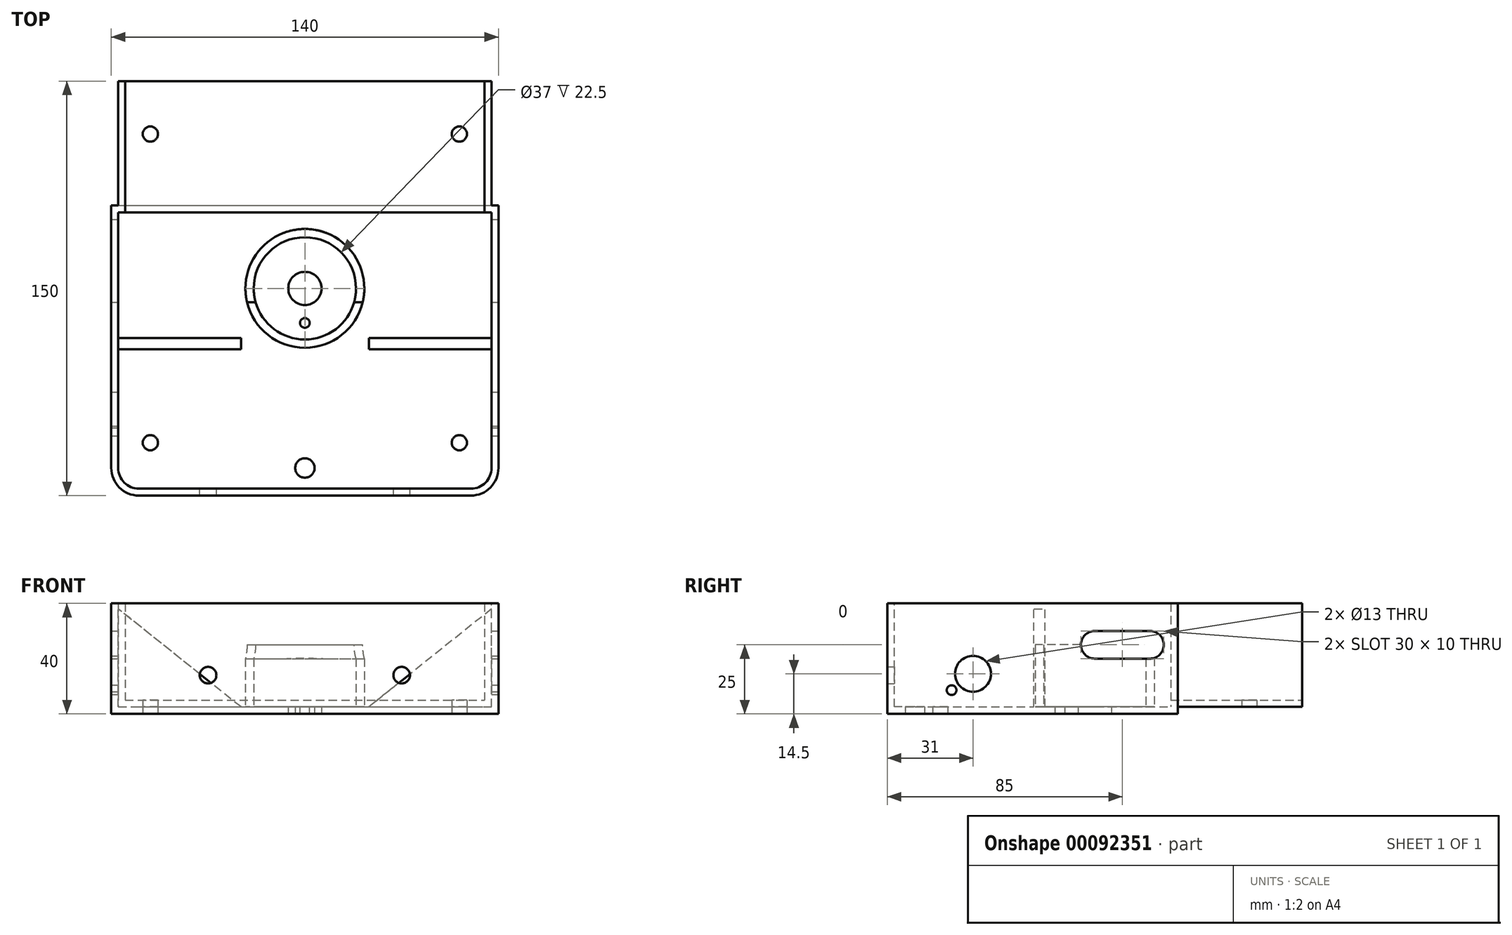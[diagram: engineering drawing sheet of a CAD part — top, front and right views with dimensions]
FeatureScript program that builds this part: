
annotation { "Feature Type Name" : "Feature", "Feature Type Description" : "" }
export const myFeature = defineFeature(function(context is Context, id is Id, definition is map)
    precondition{}
    {
        {
            var Q0;
            Q0=qCreatedBy(makeId("Top.planeOp"),FACE);
            var sketch = newSketch(context, id + "F0", { "sketchPlane" : qUnion([Q0])});
            skLineSegment(sketch, "E0.bottom", {"start": v(-70, -25) * mm, "end": v(70, -25) * mm});
            skLineSegment(sketch, "E0.top", {"start": v(-70, 125) * mm, "end": v(70, 125) * mm});
            skLineSegment(sketch, "E0.left", {"start": v(-70, -25) * mm, "end": v(-70, 125) * mm});
            skLineSegment(sketch, "E0.right", {"start": v(70, -25) * mm, "end": v(70, 125) * mm});
            skSolve(sketch);
        }
        {
            var Q0;
            Q0=makeQuery(id+"F0.imprint","IMPRINT",FACE,{"disambiguationData":[TD([[makeQuery(id+"F0.imprint","IMPRINT",EDGE,{"derivedFrom":sQuery(id+"F0.wireOp",EDGE,"E0.bottom")}),1.0]])]});
            extrude(context, id + "F1", {"entities" : qUnion([Q0]), "depth" : 40 * mm});
        }
        {
            var Q0;
            Q0=makeQuery(id+"F1.opExtrude","SWEPT_EDGE",EDGE,{"disambiguationData":[OSD([sQuery(id+"F0.wireOp",EDGE,"E0.bottom"),sQuery(id+"F0.wireOp",EDGE,"E0.left")])]});
            var Q1;
            Q1=makeQuery(id+"F1.opExtrude","SWEPT_EDGE",EDGE,{"disambiguationData":[OSD([sQuery(id+"F0.wireOp",EDGE,"E0.bottom"),sQuery(id+"F0.wireOp",EDGE,"E0.right")])]});
            fillet(context, id + "F2", {"entities" : qUnion([Q0, Q1]), "radius" : 10 * mm, "tangentPropagation" : true, "allowEdgeOverflow" : false});
        }
        {
            var Q0;
            Q0=qCreatedBy(makeId("Top.planeOp"),FACE);
            var sketch = newSketch(context, id + "F3", { "sketchPlane" : qUnion([Q0])});
            skLineSegment(sketch, "E1.bottom", {"start": v(-100, 180) * mm, "end": v(100, 180) * mm});
            skLineSegment(sketch, "E1.top", {"start": v(-100, 80) * mm, "end": v(100, 80) * mm});
            skLineSegment(sketch, "E1.left", {"start": v(-100, 180) * mm, "end": v(-100, 80) * mm});
            skLineSegment(sketch, "E1.right", {"start": v(100, 180) * mm, "end": v(100, 80) * mm});
            skSolve(sketch);
        }
        {
            var Q0;
            Q0=makeQuery(id+"F3.imprint","IMPRINT",FACE,{"disambiguationData":[TD([[makeQuery(id+"F3.imprint","IMPRINT",EDGE,{"derivedFrom":sQuery(id+"F3.wireOp",EDGE,"E1.bottom")}),-1.0]])]});
            extrude(context, id + "F4", {"entities" : qUnion([Q0]), "operationType" : NewBodyOperationType.REMOVE, "depth" : 2.5 * mm});
        }
        {
            var Q0;
            Q0=qCreatedBy(makeId("Top.planeOp"),FACE);
            var sketch = newSketch(context, id + "F5", { "sketchPlane" : qUnion([Q0])});
            skLineSegment(sketch, "E2.bottom", {"start": v(-107.5, 140) * mm, "end": v(-67.5, 140) * mm});
            skLineSegment(sketch, "E2.top", {"start": v(-107.5, 80) * mm, "end": v(-67.5, 80) * mm});
            skLineSegment(sketch, "E2.left", {"start": v(-107.5, 140) * mm, "end": v(-107.5, 80) * mm});
            skLineSegment(sketch, "E2.right", {"start": v(-67.5, 140) * mm, "end": v(-67.5, 80) * mm});
            skLineSegment(sketch, "E3.bottom", {"start": v(67.5, 140) * mm, "end": v(107.5, 140) * mm});
            skLineSegment(sketch, "E3.top", {"start": v(67.5, 80) * mm, "end": v(107.5, 80) * mm});
            skLineSegment(sketch, "E3.left", {"start": v(67.5, 140) * mm, "end": v(67.5, 80) * mm});
            skLineSegment(sketch, "E3.right", {"start": v(107.5, 140) * mm, "end": v(107.5, 80) * mm});
            skSolve(sketch);
        }
        {
            var Q0;
            Q0 = qSketchRegion(id + "F5", true);
            extrude(context, id + "F6", {"entities" : qUnion([Q0]), "operationType" : NewBodyOperationType.REMOVE, "depth" : 200 * mm});
        }
        {
            var Q0;
            Q0=makeQuery(id+"F1.opExtrude","CAP_FACE",FACE,{"disambiguationData":[OSD([sQuery(id+"F0.wireOp",EDGE,"E0.bottom"),sQuery(id+"F0.wireOp",EDGE,"E0.top"),sQuery(id+"F0.wireOp",EDGE,"E0.left"),sQuery(id+"F0.wireOp",EDGE,"E0.right")])],"isStart":false});
            var Q1;
            Q1=makeQuery(id+"F1.opExtrude","SWEPT_FACE",FACE,{"disambiguationData":[OSD([sQuery(id+"F0.wireOp",EDGE,"E0.top")])]});
            shell(context, id + "F7", {"entities" : qUnion([Q0, Q1]), "thickness" : 2.5 * mm});
        }
        {
            var Q0;
            Q0=qCreatedBy(makeId("Top.planeOp"),FACE);
            var sketch = newSketch(context, id + "F8", { "sketchPlane" : qUnion([Q0])});
            skCircle(sketch, "E4", {"center": v(0, 50) * mm, "radius": 6 * mm});
            skSolve(sketch);
        }
        {
            var Q0;
            Q0=makeQuery(id+"F8.imprint","IMPRINT",FACE,{"disambiguationData":[TD([[makeQuery(id+"F8.imprint","IMPRINT",EDGE,{"derivedFrom":sQuery(id+"F8.wireOp",EDGE,"E4")}),1.0]])]});
            extrude(context, id + "F9", {"entities" : qUnion([Q0]), "operationType" : NewBodyOperationType.REMOVE, "depth" : 25 * mm});
        }
        {
            var Q0;
            Q0=qCreatedBy(makeId("Top.planeOp"),FACE);
            var sketch = newSketch(context, id + "F10", { "sketchPlane" : qUnion([Q0])});
            skCircle(sketch, "E5", {"center": v(0, 50) * mm, "radius": 21.5 * mm});
            skCircle(sketch, "E6", {"center": v(0, 50) * mm, "radius": 18.5 * mm});
            skSolve(sketch);
        }
        {
            var Q0;
            Q0=makeQuery(id+"F10.imprint","IMPRINT",FACE,{"disambiguationData":[TD([[makeQuery(id+"F10.imprint","IMPRINT",EDGE,{"derivedFrom":sQuery(id+"F10.wireOp",EDGE,"E5")}),1.0]])]});
            extrude(context, id + "F11", {"entities" : qUnion([Q0]), "operationType" : NewBodyOperationType.ADD, "depth" : 25 * mm});
        }
        {
            var Q0;
            Q0=qCreatedBy(makeId("Top.planeOp"),FACE);
            var sketch = newSketch(context, id + "F12", { "sketchPlane" : qUnion([Q0])});
            skCircle(sketch, "E7", {"center": v(-55.86, -5.86) * mm, "radius": 2.75 * mm});
            skCircle(sketch, "E8", {"center": v(55.86, -5.86) * mm, "radius": 2.75 * mm});
            skLineSegment(sketch, "E9", {"start": v(-55.86, -5.86) * mm, "end": v(0, 50) * mm, "construction": true});
            skLineSegment(sketch, "E10", {"start": v(0, 50) * mm, "end": v(55.86, -5.86) * mm, "construction": true});
            skLineSegment(sketch, "E11", {"start": v(0, 50) * mm, "end": v(55.86, 105.86) * mm, "construction": true});
            skLineSegment(sketch, "E12", {"start": v(0, 50) * mm, "end": v(-55.86, 105.86) * mm});
            skCircle(sketch, "E13", {"center": v(0, 50) * mm, "radius": 79 * mm, "construction": true});
            skCircle(sketch, "E14", {"center": v(55.86, 105.86) * mm, "radius": 2.75 * mm});
            skCircle(sketch, "E15", {"center": v(-55.86, 105.86) * mm, "radius": 2.75 * mm});
            skSolve(sketch);
        }
        {
            var Q0;
            Q0 = qSketchRegion(id + "F12", true);
            extrude(context, id + "F13", {"entities" : qUnion([Q0]), "operationType" : NewBodyOperationType.REMOVE, "depth" : 25 * mm});
        }
        {
            var Q0;
            Q0=qCreatedBy(makeId("Right.planeOp"),FACE);
            var sketch = newSketch(context, id + "F14", { "sketchPlane" : qUnion([Q0])});
            skCircle(sketch, "E16", {"center": v(6, 14.5) * mm, "radius": 6.5 * mm});
            skSolve(sketch);
        }
        {
            var Q0;
            Q0=makeQuery(id+"F14.imprint","IMPRINT",FACE,{"disambiguationData":[TD([[makeQuery(id+"F14.imprint","IMPRINT",EDGE,{"derivedFrom":sQuery(id+"F14.wireOp",EDGE,"E16")}),1.0]])]});
            extrude(context, id + "F15", {"entities" : qUnion([Q0]), "operationType" : NewBodyOperationType.REMOVE, "oppositeDirection" : true, "depth" : 300 * mm, "hasSecondDirection" : true, "secondDirectionOppositeDirection" : false, "secondDirectionDepth" : 300 * mm});
        }
        {
            var Q0;
            Q0=qCreatedBy(makeId("Front.planeOp"),FACE);
            var sketch = newSketch(context, id + "F16", { "sketchPlane" : qUnion([Q0])});
            skCircle(sketch, "E17", {"center": v(-35, 14) * mm, "radius": 3 * mm});
            skCircle(sketch, "E18", {"center": v(35, 14) * mm, "radius": 3 * mm});
            skSolve(sketch);
        }
        {
            var Q0;
            Q0=makeQuery(id+"F16.imprint","IMPRINT",FACE,{"disambiguationData":[TD([[makeQuery(id+"F16.imprint","IMPRINT",EDGE,{"derivedFrom":sQuery(id+"F16.wireOp",EDGE,"E17")}),1.0]])]});
            var Q1;
            Q1=makeQuery(id+"F16.imprint","IMPRINT",FACE,{"disambiguationData":[TD([[makeQuery(id+"F16.imprint","IMPRINT",EDGE,{"derivedFrom":sQuery(id+"F16.wireOp",EDGE,"E18")}),1.0]])]});
            extrude(context, id + "F17", {"entities" : qUnion([Q0, Q1]), "operationType" : NewBodyOperationType.REMOVE, "depth" : 200 * mm});
        }
        {
            var Q0;
            Q0=qCreatedBy(makeId("Right.planeOp"),FACE);
            var sketch = newSketch(context, id + "F18", { "sketchPlane" : qUnion([Q0])});
            skCircle(sketch, "E19", {"center": v(6, 22) * mm, "radius": 15.5 * mm, "construction": true});
            skCircle(sketch, "E20", {"center": v(-1.75, 8.58) * mm, "radius": 1.75 * mm});
            skLineSegment(sketch, "E21", {"start": v(6, 22) * mm, "end": v(-1.75, 8.58) * mm, "construction": true});
            skLineSegment(sketch, "E22", {"start": v(6, 22) * mm, "end": v(6, -15.46) * mm, "construction": true});
            skCircle(sketch, "E23", {"center": v(6, 22) * mm, "radius": 1 * mm});
            skSolve(sketch);
        }
        {
            var Q0;
            Q0=makeQuery(id+"F18.imprint","IMPRINT",FACE,{"disambiguationData":[TD([[makeQuery(id+"F18.imprint","IMPRINT",EDGE,{"derivedFrom":sQuery(id+"F18.wireOp",EDGE,"E20")}),1.0]])]});
            extrude(context, id + "F19", {"entities" : qUnion([Q0]), "operationType" : NewBodyOperationType.REMOVE, "depth" : 400 * mm, "symmetric" : true});
        }
        {
            var Q0;
            Q0=qCreatedBy(makeId("Top.planeOp"),FACE);
            var sketch = newSketch(context, id + "F20", { "sketchPlane" : qUnion([Q0])});
            skCircle(sketch, "E24", {"center": v(0, 50) * mm, "radius": 12.5 * mm, "construction": true});
            skCircle(sketch, "E25", {"center": v(0, 37.5) * mm, "radius": 1.75 * mm});
            skSolve(sketch);
        }
        {
            var Q0;
            Q0 = qSketchRegion(id + "F20", true);
            extrude(context, id + "F21", {"entities" : qUnion([Q0]), "operationType" : NewBodyOperationType.REMOVE, "oppositeDirection" : true, "depth" : 25 * mm, "symmetric" : true});
        }
        {
            var Q0;
            Q0=qCreatedBy(makeId("Front.planeOp"),FACE);
            var sketch = newSketch(context, id + "F22", { "sketchPlane" : qUnion([Q0])});
            skLineSegment(sketch, "E26", {"start": v(-70, 0) * mm, "end": v(-20, 0) * mm});
            skLineSegment(sketch, "E27", {"start": v(-20, 0) * mm, "end": v(-70, 40) * mm});
            skLineSegment(sketch, "E28", {"start": v(-70, 40) * mm, "end": v(-70, 0) * mm});
            skLineSegment(sketch, "E29", {"start": v(20, 0) * mm, "end": v(70, 0) * mm});
            skLineSegment(sketch, "E30", {"start": v(70, 0) * mm, "end": v(70, 40) * mm});
            skLineSegment(sketch, "E31", {"start": v(70, 40) * mm, "end": v(20, 0) * mm});
            skSolve(sketch);
        }
        {
            var Q0;
            Q0 = qSketchRegion(id + "F22", true);
            extrude(context, id + "F23", {"entities" : qUnion([Q0]), "operationType" : NewBodyOperationType.ADD, "oppositeDirection" : true, "depth" : 32 * mm, "hasSecondDirection" : true, "secondDirectionOppositeDirection" : true, "secondDirectionDepth" : 28 * mm});
        }
        {
            var Q0;
            Q0=qCreatedBy(makeId("Right.planeOp"),FACE);
            var sketch = newSketch(context, id + "F24", { "sketchPlane" : qUnion([Q0])});
            skLineSegment(sketch, "E32.bottom", {"start": v(50, 30) * mm, "end": v(70, 30) * mm});
            skLineSegment(sketch, "E32.top", {"start": v(50, 20) * mm, "end": v(70, 20) * mm});
            skLineSegment(sketch, "E32.left", {"start": v(50, 30) * mm, "end": v(50, 20) * mm});
            skLineSegment(sketch, "E32.right", {"start": v(70, 30) * mm, "end": v(70, 20) * mm});
            skCircle(sketch, "E33", {"center": v(50, 25) * mm, "radius": 5 * mm});
            skCircle(sketch, "E34", {"center": v(70, 25) * mm, "radius": 5 * mm});
            skSolve(sketch);
        }
        {
            var Q0;
            {var subQ0=sQuery(id+"F24.wireOp",EDGE,"E32.left");Q0=makeQuery(id+"F24.imprint","IMPRINT",FACE,{"disambiguationData":[TD([[makeQuery(id+"F24.imprint","IMPRINT",EDGE,{"derivedFrom":subQ0}),-1.0]])]});}
            var Q1;
            {var subQ0=sQuery(id+"F24.wireOp",EDGE,"E32.left");Q1=makeQuery(id+"F24.imprint","IMPRINT",FACE,{"disambiguationData":[TD([[makeQuery(id+"F24.imprint","IMPRINT",EDGE,{"derivedFrom":subQ0}),1.0]])]});}
            var Q2;
            {var subQ0=sQuery(id+"F24.wireOp",EDGE,"E32.bottom");Q2=makeQuery(id+"F24.imprint","IMPRINT",FACE,{"disambiguationData":[TD([[makeQuery(id+"F24.imprint","IMPRINT",EDGE,{"derivedFrom":subQ0}),-1.0]])]});}
            var Q3;
            {var subQ0=sQuery(id+"F24.wireOp",EDGE,"E32.right");Q3=makeQuery(id+"F24.imprint","IMPRINT",FACE,{"disambiguationData":[TD([[makeQuery(id+"F24.imprint","IMPRINT",EDGE,{"derivedFrom":subQ0}),-1.0]])]});}
            var Q4;
            {var subQ0=sQuery(id+"F24.wireOp",EDGE,"E32.right");Q4=makeQuery(id+"F24.imprint","IMPRINT",FACE,{"disambiguationData":[TD([[makeQuery(id+"F24.imprint","IMPRINT",EDGE,{"derivedFrom":subQ0}),1.0]])]});}
            extrude(context, id + "F25", {"entities" : qUnion([Q0, Q1, Q2, Q3, Q4]), "operationType" : NewBodyOperationType.REMOVE, "oppositeDirection" : true, "depth" : 300 * mm, "symmetric" : true});
        }
        {
            var Q0;
            Q0=qCreatedBy(makeId("Top.planeOp"),FACE);
            var sketch = newSketch(context, id + "F26", { "sketchPlane" : qUnion([Q0])});
            skCircle(sketch, "E35", {"center": v(0, -15) * mm, "radius": 3.5 * mm});
            skSolve(sketch);
        }
        {
            var Q0;
            Q0 = qSketchRegion(id + "F26", true);
            extrude(context, id + "F27", {"entities" : qUnion([Q0]), "operationType" : NewBodyOperationType.REMOVE, "depth" : 25 * mm});
        }
    });
